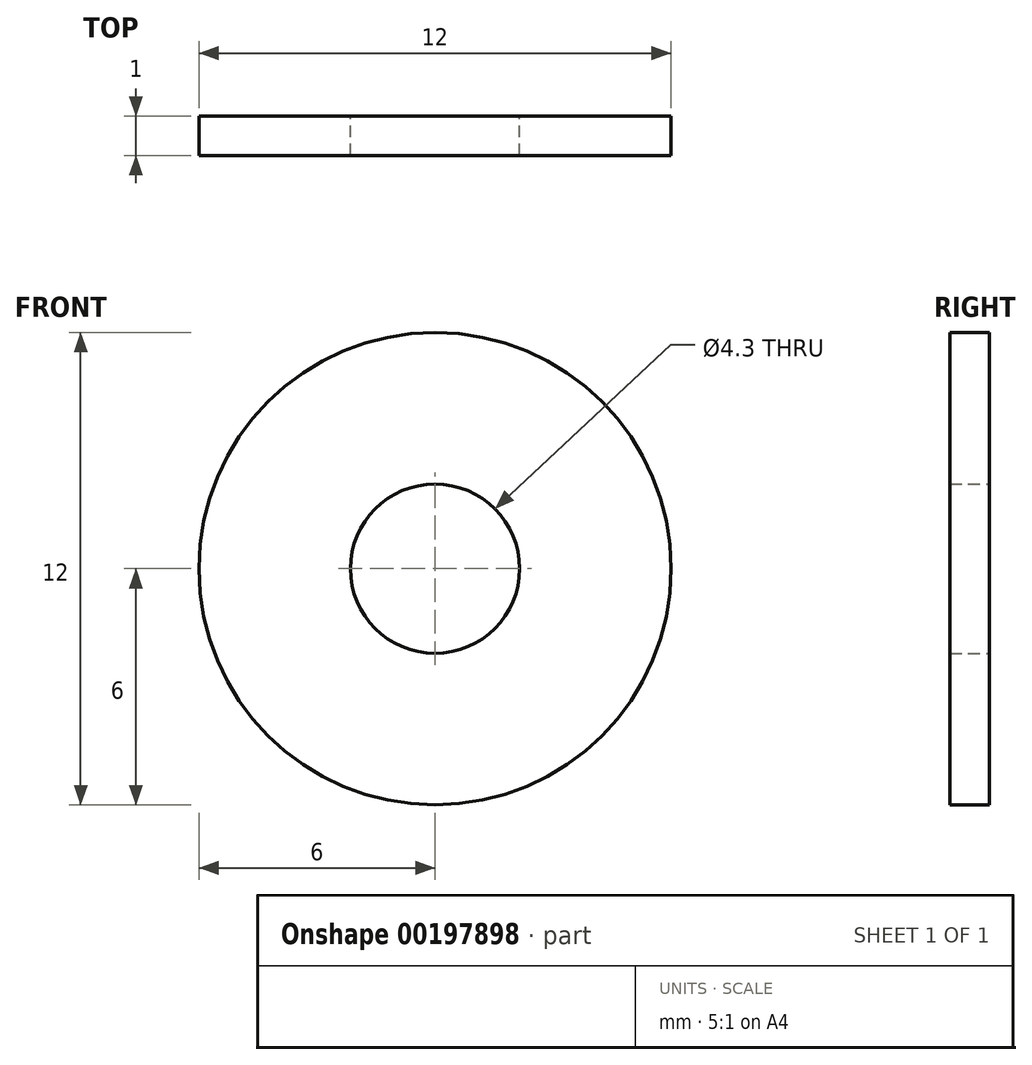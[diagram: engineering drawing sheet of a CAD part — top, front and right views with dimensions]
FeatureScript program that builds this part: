
annotation { "Feature Type Name" : "Feature", "Feature Type Description" : "" }
export const myFeature = defineFeature(function(context is Context, id is Id, definition is map)
    precondition{}
    {
        {
            var Q0;
            Q0=qCreatedBy(makeId("Front.planeOp"),FACE);
            var sketch = newSketch(context, id + "F0", { "sketchPlane" : qUnion([Q0])});
            skCircle(sketch, "E0", {"center": v(0, 0) * mm, "radius": 6 * mm});
            skCircle(sketch, "E1", {"center": v(0, 0) * mm, "radius": 2.15 * mm});
            skSolve(sketch);
        }
        {
            var Q0;
            Q0=makeQuery(id+"F0.imprint","IMPRINT",FACE,{"disambiguationData":[TD([[makeQuery(id+"F0.imprint","IMPRINT",EDGE,{"derivedFrom":sQuery(id+"F0.wireOp",EDGE,"E0")}),1.0]])]});
            extrude(context, id + "F1", {"entities" : qUnion([Q0]), "depth" : 1 * mm, "symmetric" : true});
        }
    });
